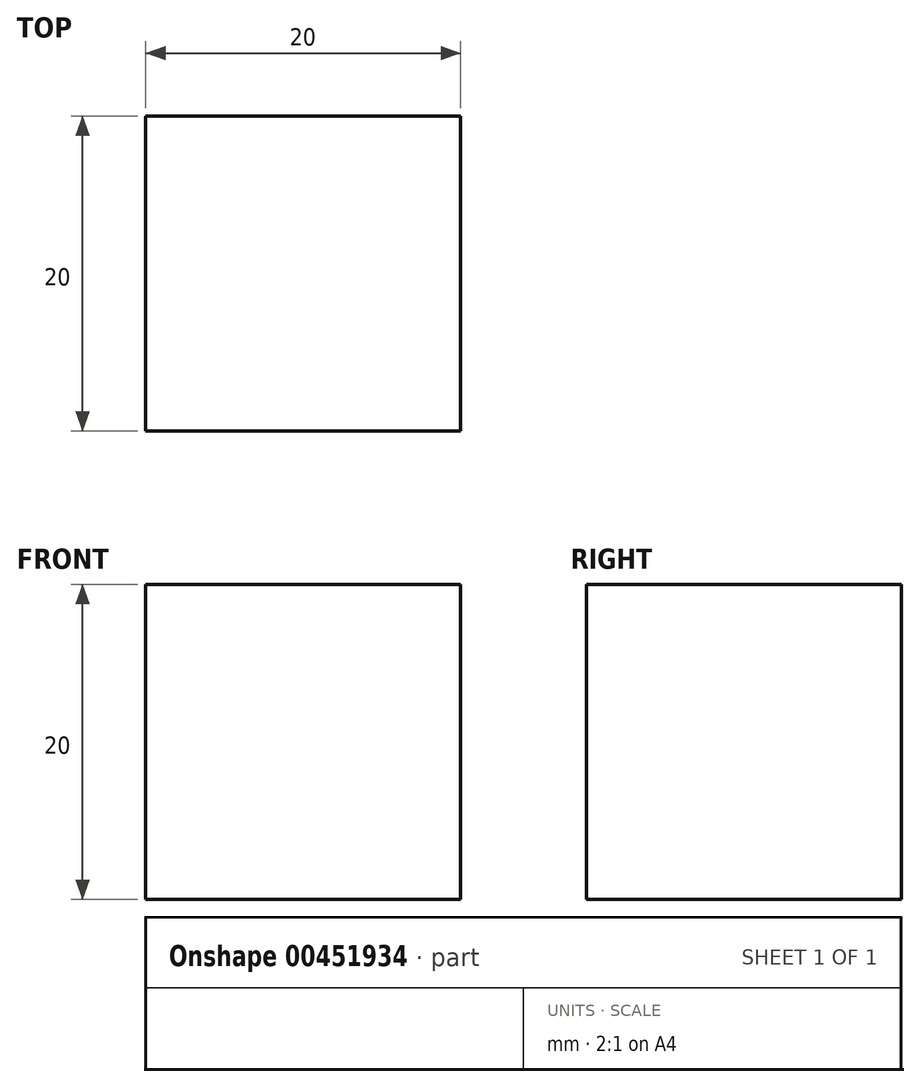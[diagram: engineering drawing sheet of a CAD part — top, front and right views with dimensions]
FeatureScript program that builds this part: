
annotation { "Feature Type Name" : "Feature", "Feature Type Description" : "" }
export const myFeature = defineFeature(function(context is Context, id is Id, definition is map)
    precondition{}
    {
        {
            var Q0;
            Q0=qCreatedBy(makeId("Front.planeOp"),FACE);
            var sketch = newSketch(context, id + "F0", { "sketchPlane" : qUnion([Q0])});
            skLineSegment(sketch, "E0.bottom", {"start": v(0, 20) * mm, "end": v(20, 20) * mm});
            skLineSegment(sketch, "E0.top", {"start": v(0, 0) * mm, "end": v(20, 0) * mm});
            skLineSegment(sketch, "E0.left", {"start": v(0, 20) * mm, "end": v(0, 0) * mm});
            skLineSegment(sketch, "E0.right", {"start": v(20, 20) * mm, "end": v(20, 0) * mm});
            skSolve(sketch);
        }
        {
            var Q0;
            Q0 = qSketchRegion(id + "F0", true);
            extrude(context, id + "F1", {"entities" : qUnion([Q0]), "depth" : 20 * mm});
        }
    });
